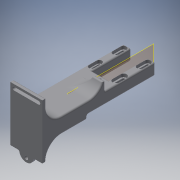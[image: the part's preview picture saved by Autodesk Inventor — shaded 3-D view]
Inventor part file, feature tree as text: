
AUTODESK INVENTOR PART (.ipt)
format: ipt  version: 2016 (Build 200138000, 138)  size: 529,408 bytes
history: native  units: mm
features: sketch x9, extrude x8, fillet x8, projected_geometry x7, chamfer x3, plane x2, mirror x1, revolve x1
ambient origin geometry x8: Origin, YZ Plane, XZ Plane, XY Plane, X Axis, Y Axis, Z Axis, Center Point
bodies: Solid1 (feature_tree)
feature tree (39):
  extrude  "Extrusion1"  Depth=10.0mm
  plane  "Work Plane2"
  extrude  "Extrusion3"  Depth=10.0mm
  mirror  "Mirror4"
  extrude  "Extrusion4"  Depth=41.0mm
  extrude  "Extrusion5"  Depth=5.0mm
  extrude  "Extrusion6"  Depth=31.0mm
  fillet  "Fillet1"  Radius=20.0mm
  fillet  "Fillet2"  Radius=21.0mm
  extrude  "Extrusion7"  Depth=1.333333mm
  plane  "Work Plane5"
  sketch  "Sketch9"  dims[d17=20.0mm d18=0.0mm d19=1.333333mm]
  revolve  "Revolution1"  [1 undecoded]
  extrude  "Extrusion9"  Depth=4.0mm TaperAngle=0.0deg
  extrude  "Extrusion10"  Depth=5.0mm
  fillet  "Fillet5"  Radius=4.0mm
  fillet  "Fillet8"  Radius=20.0mm
  fillet  "Fillet9"  Radius=20.0mm
  fillet  "Fillet7"  Radius=12.0mm
  chamfer  "Chamfer1"  Distance=20.0mm
  chamfer  "Chamfer2"  Distance=1.0mm
  fillet  "Fillet10"  Radius=4.0mm
  fillet  "Fillet12"  Radius=4.0mm
  chamfer  "Chamfer3"  [1 undecoded]
  sketch  "Sketch1"  dims[d0=145.0mm d1=10.0mm]
  sketch  "Sketch3"  dims[d3=20.0mm d4=0.0mm d5=10.0mm]
  projected_geometry  "Projected Loop1"
  sketch  "Sketch4"  dims[d6=4.0mm d9=41.0mm]
  projected_geometry  "Projected Loop2"
  sketch  "Sketch5"  dims[d10=50.0mm d11=5.0mm]
  projected_geometry  "Projected Loop3"
  sketch  "Sketch6"  dims[d12=10.0mm d13=31.0mm d14=20.0mm d15=0.0mm d16=21.0mm]
  projected_geometry  "Projected Loop4"
  projected_geometry  "Projected Loop5"
  sketch  "Sketch10"  dims[d20=1.72678mm d21=2.027682mm]
  sketch  "Sketch12"  dims[d22=1.666667mm d23=4.0mm d24=0.0mm]
  projected_geometry  "Projected Loop9"
  sketch  "Sketch13"  dims[d25=30.0mm d26=5.0mm d27=4.0mm d28=0.0mm d29=20.0mm d30=20.0mm d32=12.0mm d33=0.0mm d40=20.0mm d42=1.0mm d43=4.0mm d44=2.0mm d45=45.0deg d46=4.0mm d47=2.0mm d48=45.0deg d49=-13.089969mm d50=1.4mm d51=90.0deg d54=12.0mm d56=3.0mm d57=20.0mm d58=2.0mm d59=2.0mm d62=4.2mm d63=4.75mm d64=4.75mm d65=10.0mm d66=0.0mm d68=4.5mm d69=4.0mm d70=20.5mm d71=18.0mm d72=10.0mm d73=0.0mm d74=2.0mm d75=2.0mm d76=45.0deg d77=2.0mm d78=14.365114mm]
  projected_geometry  "Projected Loop10"
note: 2 required parameter values undecoded (feature->parameter linkage not recoverable at this tier; creation-order binding heuristic only, values carry confidence <= 0.55)